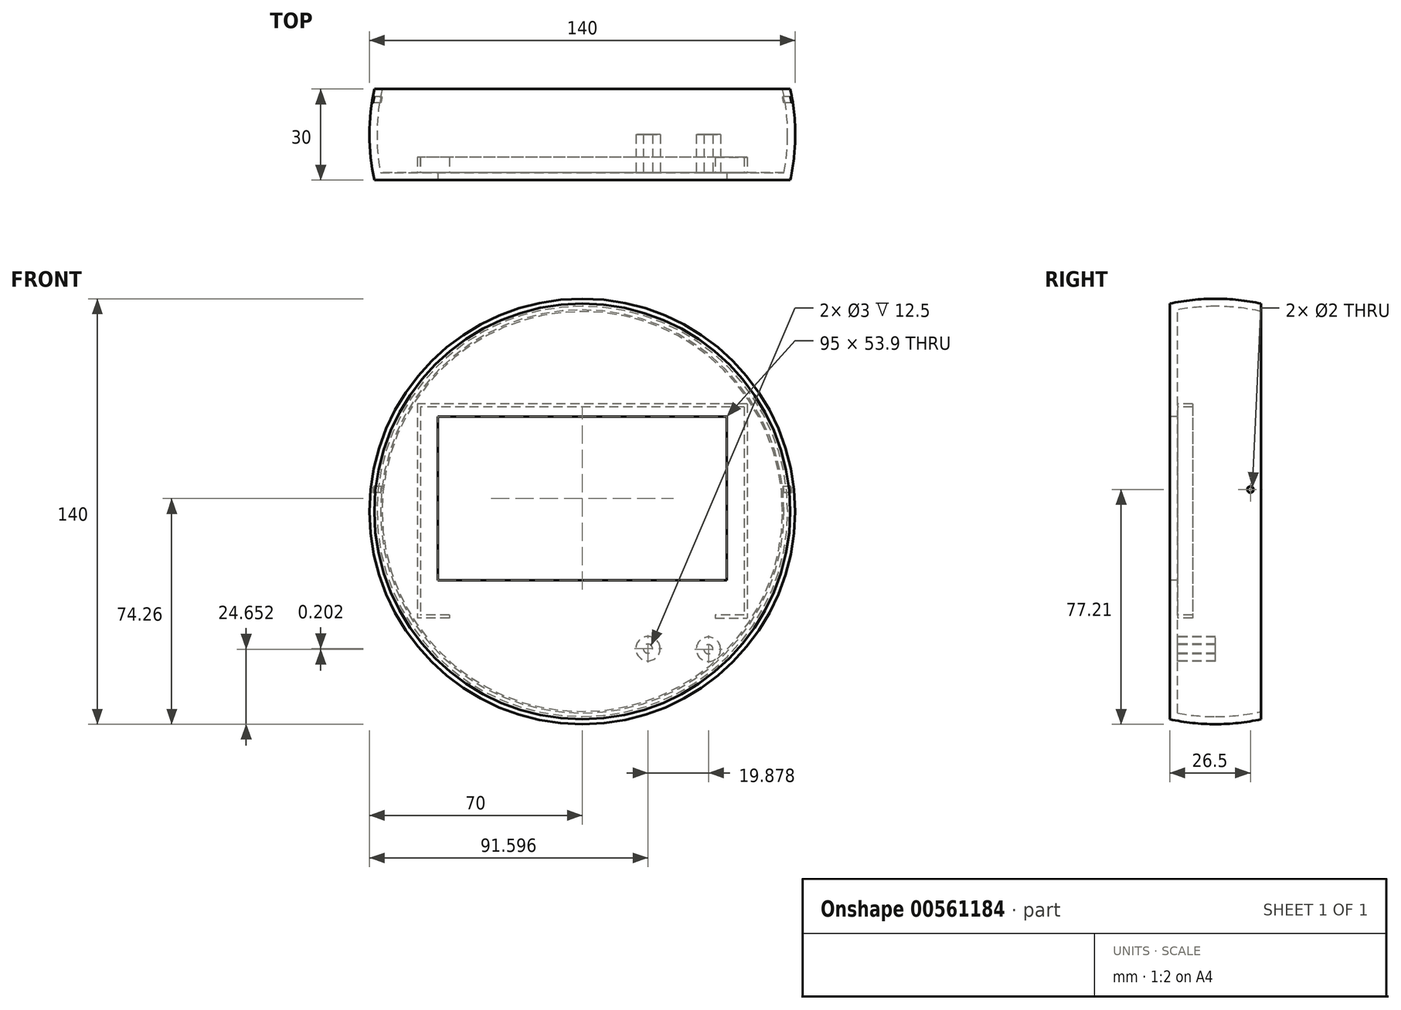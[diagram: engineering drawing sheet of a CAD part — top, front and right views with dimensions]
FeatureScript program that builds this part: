
annotation { "Feature Type Name" : "Feature", "Feature Type Description" : "" }
export const myFeature = defineFeature(function(context is Context, id is Id, definition is map)
    precondition{}
    {
        {
            var Q0;
            Q0=qCreatedBy(makeId("Front.planeOp"),FACE);
            var sketch = newSketch(context, id + "F0", { "sketchPlane" : qUnion([Q0])});
            skLineSegment(sketch, "E0", {"start": v(0, 62.79) * mm, "end": v(0, -77.21) * mm});
            skArc(sketch, "E1", {"start": v(0, 62.79) * mm, "mid": v(-70, -7.21) * mm, "end": v(0, -77.21) * mm});
            skSolve(sketch);
        }
        {
            var Q0;
            Q0=qSketchRegion(id+"F0",true);
            var Q1;
            Q1=sQuery(id+"F0.wireOp",EDGE,"E0");
            revolve(context, id + "F1", {"entities" : qUnion([Q0]), "axis" : qUnion([Q1]), "revolveType" : RevolveType.FULL});
        }
        {
            var Q0;
            Q0=qCreatedBy(makeId("Front.planeOp"),FACE);
            cPlane(context, id + "F2", {"entities" : qUnion([Q0]), "cplaneType" : CPlaneType.OFFSET, "offset" : 15 * mm, "width" : 150 * mm, "height" : 150 * mm});
        }
        {
            var Q0;
            Q0=qCreatedBy(id+"F2.planeOp",FACE);
            var sketch = newSketch(context, id + "F3", { "sketchPlane" : qUnion([Q0])});
            skLineSegment(sketch, "E2.bottom", {"start": v(-79.17, 75.12) * mm, "end": v(80.31, 75.12) * mm});
            skLineSegment(sketch, "E2.top", {"start": v(-79.17, -85.38) * mm, "end": v(80.31, -85.38) * mm});
            skLineSegment(sketch, "E2.left", {"start": v(-79.17, 75.12) * mm, "end": v(-79.17, -85.38) * mm});
            skLineSegment(sketch, "E2.right", {"start": v(80.31, 75.12) * mm, "end": v(80.31, -85.38) * mm});
            skSolve(sketch);
        }
        {
            var Q0;
            Q0=makeQuery(id+"F3.imprint","IMPRINT",FACE,{"disambiguationData":[TD([[makeQuery(id+"F3.imprint","IMPRINT",EDGE,{"derivedFrom":sQuery(id+"F3.wireOp",EDGE,"E2.bottom")}),-1.0]])]});
            extrude(context, id + "F4", {"entities" : qUnion([Q0]), "operationType" : NewBodyOperationType.REMOVE, "depth" : 80 * mm, "offsetDistance" : 25 * mm});
        }
        {
            var Q0;
            Q0=qCreatedBy(makeId("Front.planeOp"),FACE);
            cPlane(context, id + "F5", {"entities" : qUnion([Q0]), "cplaneType" : CPlaneType.OFFSET, "offset" : 15 * mm, "oppositeDirection" : true, "width" : 150 * mm, "height" : 150 * mm});
        }
        {
            var Q0;
            Q0=qCreatedBy(id+"F5.planeOp",FACE);
            var sketch = newSketch(context, id + "F6", { "sketchPlane" : qUnion([Q0])});
            skLineSegment(sketch, "E3.bottom", {"start": v(-72.3, 70.13) * mm, "end": v(72.81, 70.13) * mm});
            skLineSegment(sketch, "E3.top", {"start": v(-72.3, -80.74) * mm, "end": v(72.81, -80.74) * mm});
            skLineSegment(sketch, "E3.left", {"start": v(-72.3, 70.13) * mm, "end": v(-72.3, -80.74) * mm});
            skLineSegment(sketch, "E3.right", {"start": v(72.81, 70.13) * mm, "end": v(72.81, -80.74) * mm});
            skSolve(sketch);
        }
        {
            var Q0;
            Q0=makeQuery(id+"F6.imprint","IMPRINT",FACE,{"disambiguationData":[TD([[makeQuery(id+"F6.imprint","IMPRINT",EDGE,{"derivedFrom":sQuery(id+"F6.wireOp",EDGE,"E3.bottom")}),-1.0]])]});
            extrude(context, id + "F7", {"entities" : qUnion([Q0]), "operationType" : NewBodyOperationType.REMOVE, "oppositeDirection" : true, "depth" : 60 * mm, "offsetDistance" : 25 * mm});
        }
        {
            var Q0;
            Q0=makeQuery(id+"F7.boolean.opBoolean","COPY",FACE,{"derivedFrom":makeQuery(id+"F7.opExtrude","CAP_FACE",FACE,{"disambiguationData":[OSD([sQuery(id+"F6.wireOp",EDGE,"E3.bottom"),sQuery(id+"F6.wireOp",EDGE,"E3.top"),sQuery(id+"F6.wireOp",EDGE,"E3.left"),sQuery(id+"F6.wireOp",EDGE,"E3.right")])],"isStart":true})});
            shell(context, id + "F8", {"entities" : qUnion([Q0]), "thickness" : 2.5 * mm});
        }
        {
            var Q0;
            Q0=qCreatedBy(id+"F2.planeOp",FACE);
            var sketch = newSketch(context, id + "F9", { "sketchPlane" : qUnion([Q0])});
            skPoint(sketch, "E4.middle", {"position": v(0, 0) * mm});
            skLineSegment(sketch, "E5.bottom", {"start": v(47.5, 24) * mm, "end": v(-47.5, 24) * mm});
            skLineSegment(sketch, "E5.top", {"start": v(47.5, -29.9) * mm, "end": v(-47.5, -29.9) * mm});
            skLineSegment(sketch, "E5.left", {"start": v(47.5, 24) * mm, "end": v(47.5, -29.9) * mm});
            skLineSegment(sketch, "E5.right", {"start": v(-47.5, 24) * mm, "end": v(-47.5, -29.9) * mm});
            skSolve(sketch);
        }
        {
            var Q0;
            Q0=qSketchRegion(id+"F9",true);
            extrude(context, id + "F10", {"entities" : qUnion([Q0]), "operationType" : NewBodyOperationType.REMOVE, "oppositeDirection" : true, "depth" : 10 * mm, "offsetDistance" : 25 * mm});
        }
        {
            var Q0;
            Q0=qCreatedBy(makeId("Right.planeOp"),FACE);
            var sketch = newSketch(context, id + "F11", { "sketchPlane" : qUnion([Q0])});
            skCircle(sketch, "E6", {"center": v(11.5, 0) * mm, "radius": 1 * mm});
            skSolve(sketch);
        }
        {
            var Q0;
            Q0=qSketchRegion(id+"F11",true);
            extrude(context, id + "F12", {"entities" : qUnion([Q0]), "operationType" : NewBodyOperationType.REMOVE, "endBound" : BoundingType.SYMMETRIC, "depth" : 150 * mm, "offsetDistance" : 25 * mm});
        }
        {
            var Q0;
            Q0=qCreatedBy(id+"F2.planeOp",FACE);
            var sketch = newSketch(context, id + "F13", { "sketchPlane" : qUnion([Q0])});
            skPoint(sketch, "E7.middle", {"position": v(0, -42.38) * mm});
            skPoint(sketch, "E8.middle", {"position": v(54.46, -5.61) * mm});
            skPoint(sketch, "E9.middle", {"position": v(0, 28.35) * mm});
            skLineSegment(sketch, "E10.bottom", {"start": v(53.27, 27.2) * mm, "end": v(-53.23, 27.2) * mm});
            skLineSegment(sketch, "E10.left", {"start": v(53.27, 27.2) * mm, "end": v(53.23, -41.3) * mm});
            skLineSegment(sketch, "E10.right", {"start": v(-53.23, 27.2) * mm, "end": v(-53.27, -41.3) * mm});
            skPoint(sketch, "E10.middle", {"position": v(0, -7.04) * mm});
            skLineSegment(sketch, "E11.bottom", {"start": v(54.25, 28.2) * mm, "end": v(-54.25, 28.2) * mm});
            skLineSegment(sketch, "E11.left", {"start": v(54.25, 28.2) * mm, "end": v(54.25, -42.3) * mm});
            skLineSegment(sketch, "E11.right", {"start": v(-54.25, 28.2) * mm, "end": v(-54.25, -42.3) * mm});
            skLineSegment(sketch, "E12", {"start": v(53.23, -41.3) * mm, "end": v(43.68, -41.3) * mm});
            skLineSegment(sketch, "E13", {"start": v(43.68, -41.3) * mm, "end": v(43.68, -42.3) * mm});
            skLineSegment(sketch, "E14", {"start": v(43.68, -42.3) * mm, "end": v(54.25, -42.3) * mm});
            skLineSegment(sketch, "E15.MirrorCS", {"start": v(-43.68, -42.3) * mm, "end": v(-54.25, -42.3) * mm});
            skLineSegment(sketch, "E16.MirrorCS", {"start": v(-43.68, -41.3) * mm, "end": v(-43.68, -42.3) * mm});
            skLineSegment(sketch, "E17", {"start": v(-43.68, -41.3) * mm, "end": v(-53.27, -41.3) * mm});
            skSolve(sketch);
        }
        {
            var Q0;
            Q0=qSketchRegion(id+"F13",true);
            extrude(context, id + "F14", {"entities" : qUnion([Q0]), "operationType" : NewBodyOperationType.ADD, "oppositeDirection" : true, "depth" : 7.5 * mm, "offsetDistance" : 25 * mm});
        }
        {
            var Q0;
            Q0=qCreatedBy(id+"F2.planeOp",FACE);
            var sketch = newSketch(context, id + "F15", { "sketchPlane" : qUnion([Q0])});
            skCircle(sketch, "E18", {"center": v(41.47, -52.56) * mm, "radius": 4 * mm});
            skCircle(sketch, "E19", {"center": v(21.6, -52.36) * mm, "radius": 4 * mm});
            skCircle(sketch, "E20", {"center": v(41.47, -52.56) * mm, "radius": 1.5 * mm});
            skCircle(sketch, "E21", {"center": v(21.6, -52.36) * mm, "radius": 1.5 * mm});
            skSolve(sketch);
        }
        {
            var Q0;
            Q0 = qSketchRegion(id + "F15", true);
            extrude(context, id + "F16", {"entities" : qUnion([Q0]), "operationType" : NewBodyOperationType.ADD, "oppositeDirection" : true, "depth" : 15 * mm, "offsetDistance" : 25 * mm});
        }
    });
